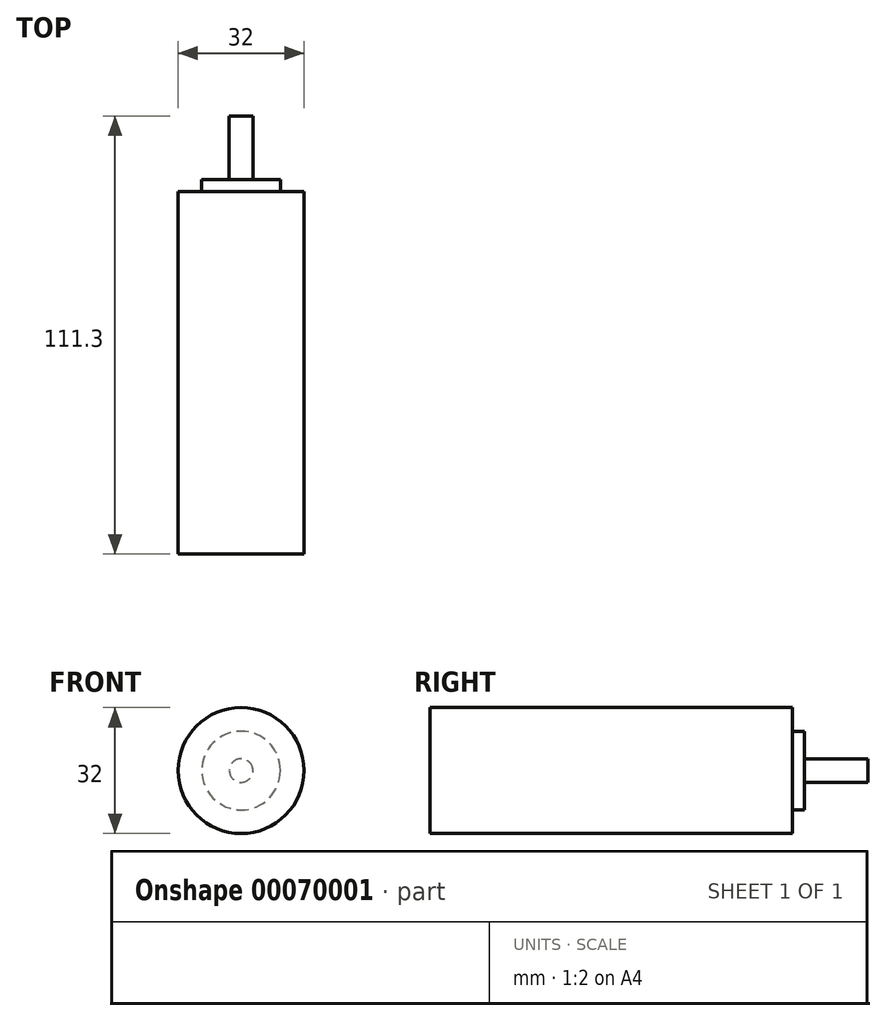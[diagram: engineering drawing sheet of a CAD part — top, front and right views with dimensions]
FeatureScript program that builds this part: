
annotation { "Feature Type Name" : "Feature", "Feature Type Description" : "" }
export const myFeature = defineFeature(function(context is Context, id is Id, definition is map)
    precondition{}
    {
        {
            var Q0;
            Q0=qCreatedBy(makeId("Front.planeOp"),FACE);
            var sketch = newSketch(context, id + "F0", { "sketchPlane" : qUnion([Q0])});
            skCircle(sketch, "E0", {"center": v(0, 0) * mm, "radius": 10 * mm});
            skSolve(sketch);
        }
        {
            var Q0;
            Q0=qCreatedBy(makeId("Front.planeOp"),FACE);
            var sketch = newSketch(context, id + "F1", { "sketchPlane" : qUnion([Q0])});
            skCircle(sketch, "E1", {"center": v(0, 0) * mm, "radius": 16 * mm});
            skSolve(sketch);
        }
        {
            var Q0;
            Q0=qCreatedBy(makeId("Front.planeOp"),FACE);
            var sketch = newSketch(context, id + "F2", { "sketchPlane" : qUnion([Q0])});
            skCircle(sketch, "E2", {"center": v(0, 0) * mm, "radius": 3 * mm});
            skSolve(sketch);
        }
        {
            var Q0;
            Q0 = qSketchRegion(id + "F0", true);
            extrude(context, id + "F3", {"entities" : qUnion([Q0]), "oppositeDirection" : true, "depth" : 3 * mm});
        }
        {
            var Q0;
            Q0 = qSketchRegion(id + "F2", true);
            extrude(context, id + "F4", {"entities" : qUnion([Q0]), "operationType" : NewBodyOperationType.ADD, "oppositeDirection" : true, "depth" : 19.2 * mm});
        }
        {
            var Q0;
            Q0 = qSketchRegion(id + "F1", true);
            extrude(context, id + "F5", {"entities" : qUnion([Q0]), "operationType" : NewBodyOperationType.ADD, "depth" : 92.1 * mm});
        }
    });
